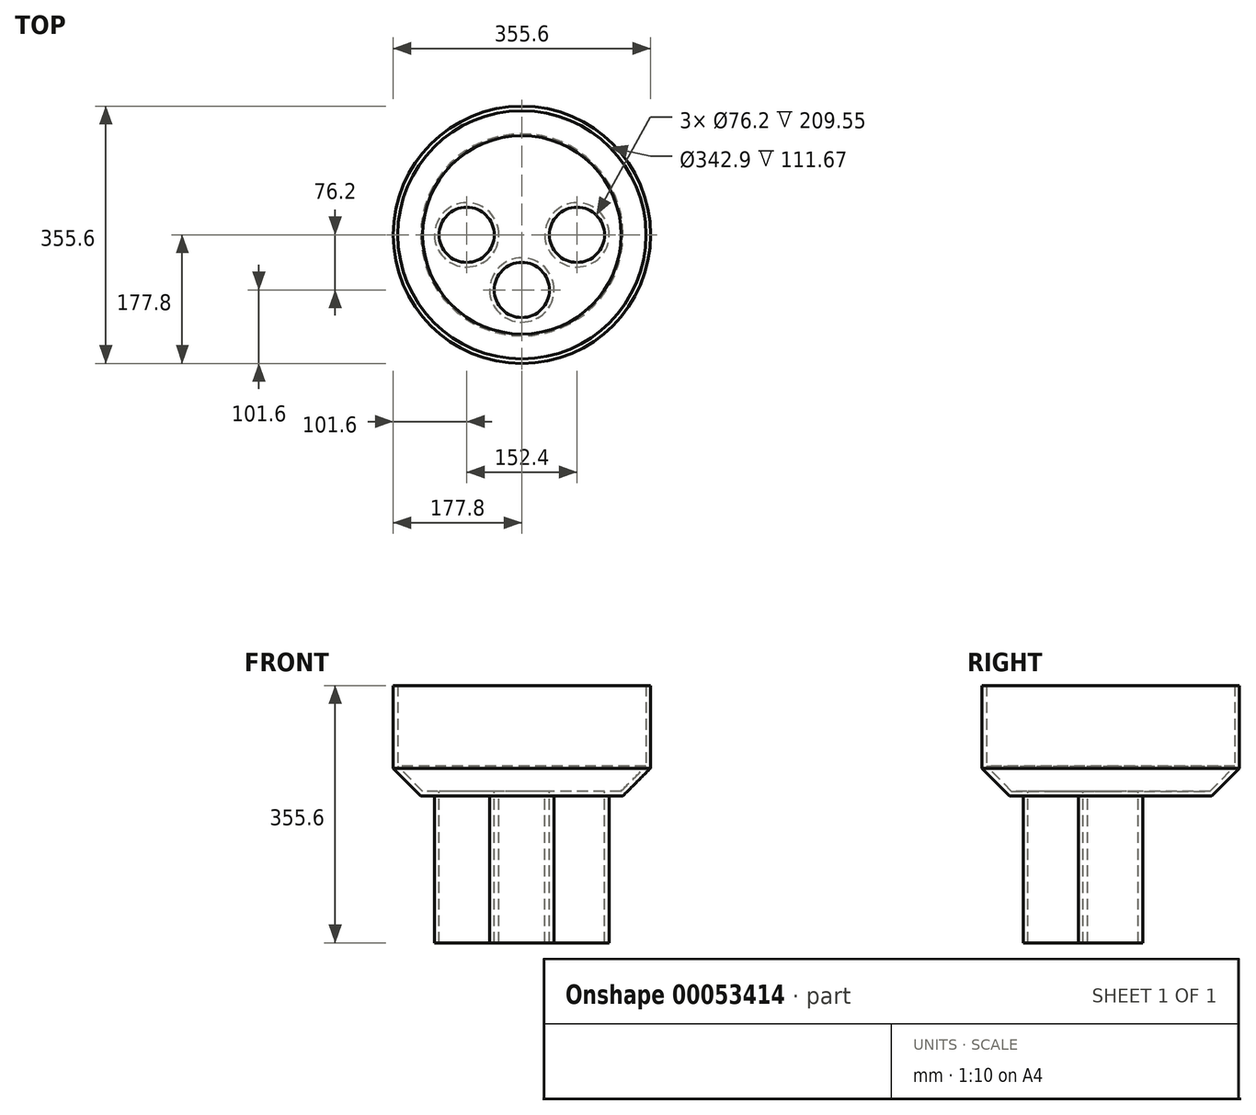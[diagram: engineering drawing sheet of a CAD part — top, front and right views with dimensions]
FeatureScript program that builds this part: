
annotation { "Feature Type Name" : "Feature", "Feature Type Description" : "" }
export const myFeature = defineFeature(function(context is Context, id is Id, definition is map)
    precondition{}
    {
        {
            var Q0;
            Q0=qCreatedBy(makeId("Top.planeOp"),FACE);
            var sketch = newSketch(context, id + "F0", { "sketchPlane" : qUnion([Q0])});
            skCircle(sketch, "E0", {"center": v(0, 0) * mm, "radius": 177.8 * mm});
            skSolve(sketch);
        }
        {
            var Q0;
            Q0 = qSketchRegion(id + "F0", true);
            extrude(context, id + "F1", {"entities" : qUnion([Q0]), "depth" : 152.4 * mm});
        }
        {
            var Q0;
            Q0=makeQuery(id+"F1.opExtrude","CAP_FACE",FACE,{"disambiguationData":[OSD([sQuery(id+"F0.wireOp",EDGE,"E0")])],"isStart":true});
            var sketch = newSketch(context, id + "F2", { "sketchPlane" : qUnion([Q0])});
            skCircle(sketch, "E1", {"center": v(76.2, 0) * mm, "radius": 44.45 * mm});
            skCircle(sketch, "E2", {"center": v(0, 76.2) * mm, "radius": 44.45 * mm});
            skCircle(sketch, "E3", {"center": v(-76.2, 0) * mm, "radius": 44.45 * mm});
            skSolve(sketch);
        }
        {
            var Q0;
            Q0 = qSketchRegion(id + "F2", true);
            extrude(context, id + "F3", {"entities" : qUnion([Q0]), "operationType" : NewBodyOperationType.ADD, "depth" : 209.55 * mm});
        }
        {
            var Q0;
            Q0=makeQuery(id+"F1.opExtrude","CAP_EDGE",EDGE,{"disambiguationData":[OSD([sQuery(id+"F0.wireOp",EDGE,"E0")])],"isStart":true});
            chamfer(context, id + "F4", {"entities" : qUnion([Q0]), "width" : 38.1 * mm, "tangentPropagation" : true});
        }
        {
            var Q0;
            Q0=makeQuery(id+"F1.opExtrude","CAP_FACE",FACE,{"disambiguationData":[OSD([sQuery(id+"F0.wireOp",EDGE,"E0")])],"isStart":false});
            shell(context, id + "F5", {"entities" : qUnion([Q0]), "thickness" : 6.35 * mm});
        }
        {
            var Q0;
            Q0=makeQuery(id+"F3.opExtrude","CAP_FACE",FACE,{"disambiguationData":[OSD([sQuery(id+"F2.wireOp",EDGE,"E3")])],"isStart":false});
            var sketch = newSketch(context, id + "F6", { "sketchPlane" : qUnion([Q0])});
            skCircle(sketch, "E4", {"center": v(0, 0) * mm, "radius": 132.7 * mm});
            skSolve(sketch);
        }
        {
            var Q0;
            Q0 = qSketchRegion(id + "F6", true);
            extrude(context, id + "F7", {"entities" : qUnion([Q0]), "operationType" : NewBodyOperationType.REMOVE, "oppositeDirection" : true, "depth" : 6.35 * mm});
        }
    });
